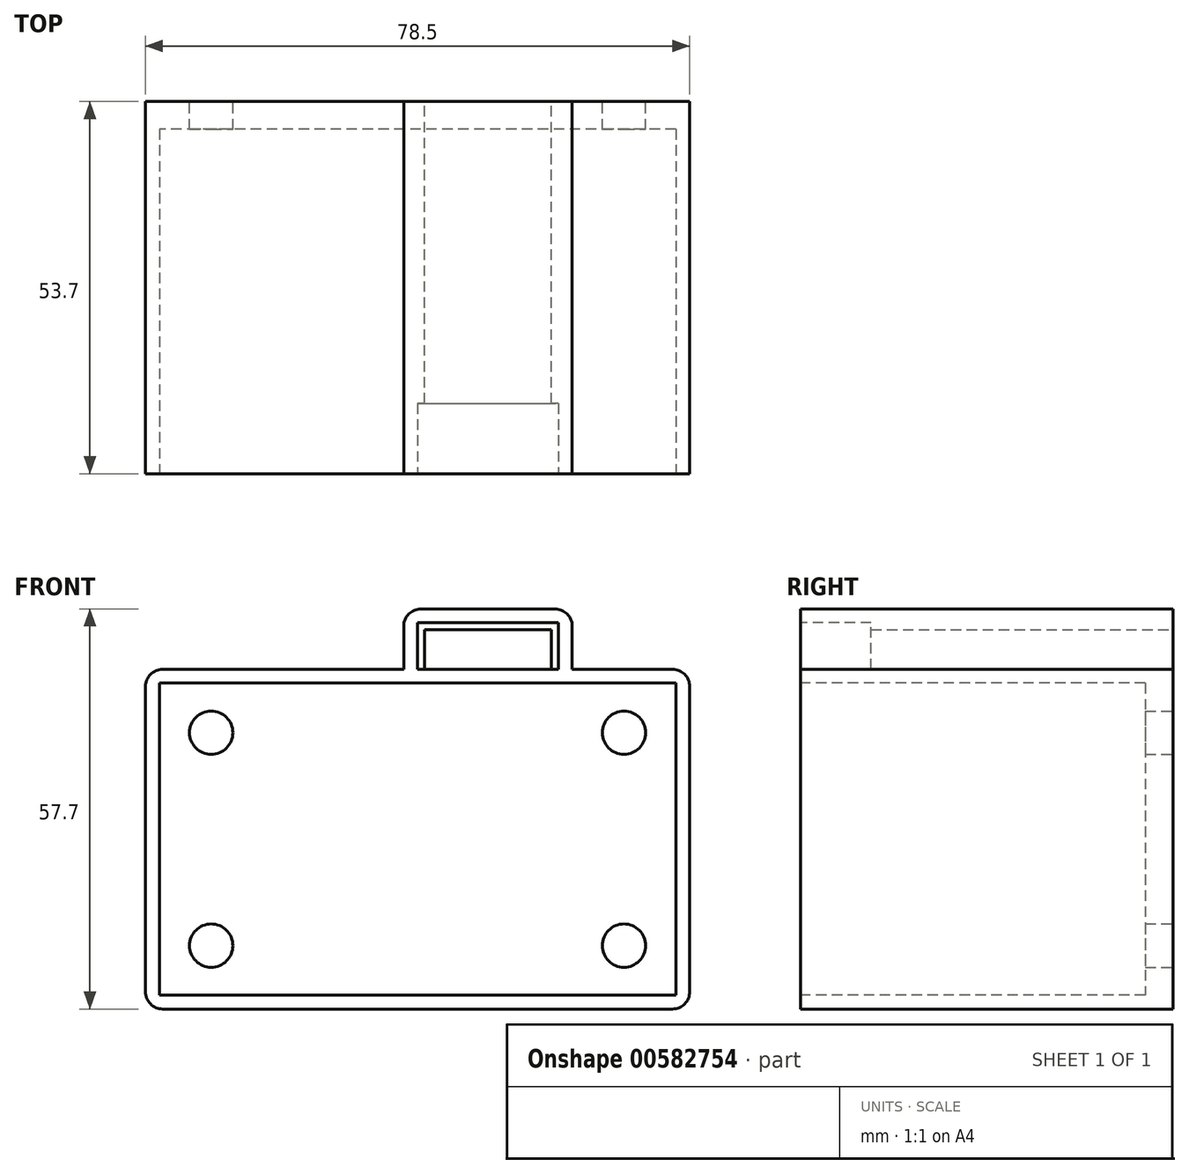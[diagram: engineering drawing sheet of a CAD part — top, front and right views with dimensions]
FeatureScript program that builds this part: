
annotation { "Feature Type Name" : "Feature", "Feature Type Description" : "" }
export const myFeature = defineFeature(function(context is Context, id is Id, definition is map)
    precondition{}
    {
        {
            var Q0;
            Q0=qCreatedBy(makeId("Front.planeOp"),FACE);
            var sketch = newSketch(context, id + "F0", { "sketchPlane" : qUnion([Q0])});
            skLineSegment(sketch, "E0.bottom", {"start": v(37.25, 22.5) * mm, "end": v(-37.25, 22.5) * mm});
            skLineSegment(sketch, "E0.top", {"start": v(37.25, -22.5) * mm, "end": v(-37.25, -22.5) * mm});
            skLineSegment(sketch, "E0.left", {"start": v(37.25, 22.5) * mm, "end": v(37.25, -22.5) * mm});
            skLineSegment(sketch, "E0.right", {"start": v(-37.25, 22.5) * mm, "end": v(-37.25, -22.5) * mm});
            skPoint(sketch, "E0.middle", {"position": v(0, 0) * mm});
            skLineSegment(sketch, "E1.0", {"start": v(39.25, 24.5) * mm, "end": v(-39.25, 24.5) * mm});
            skLineSegment(sketch, "E1.1", {"start": v(39.25, 24.5) * mm, "end": v(39.25, -24.5) * mm});
            skLineSegment(sketch, "E1.2", {"start": v(39.25, -24.5) * mm, "end": v(-39.25, -24.5) * mm});
            skLineSegment(sketch, "E1.3", {"start": v(-39.25, 24.5) * mm, "end": v(-39.25, -24.5) * mm});
            skSolve(sketch);
        }
        {
            var Q0;
            Q0 = qSketchRegion(id + "F0", true);
            extrude(context, id + "F1", {"entities" : qUnion([Q0]), "oppositeDirection" : true, "depth" : 53.7 * mm, "offsetDistance" : 25 * mm});
        }
        {
            var Q0;
            Q0=qCreatedBy(makeId("Front.planeOp"),FACE);
            var sketch = newSketch(context, id + "F2", { "sketchPlane" : qUnion([Q0])});
            skLineSegment(sketch, "E2.bottom", {"start": v(0, 24.5) * mm, "end": v(20.3, 24.5) * mm});
            skLineSegment(sketch, "E2.top", {"start": v(0, 31.2) * mm, "end": v(20.3, 31.2) * mm});
            skLineSegment(sketch, "E2.left", {"start": v(0, 24.5) * mm, "end": v(0, 31.2) * mm});
            skLineSegment(sketch, "E2.right", {"start": v(20.3, 24.5) * mm, "end": v(20.3, 31.2) * mm});
            skLineSegment(sketch, "E3.0", {"start": v(-2, 33.2) * mm, "end": v(22.3, 33.2) * mm});
            skLineSegment(sketch, "E3.1", {"start": v(-2, 22.5) * mm, "end": v(-2, 33.2) * mm});
            skLineSegment(sketch, "E3.2", {"start": v(-2, 22.5) * mm, "end": v(22.3, 22.5) * mm});
            skLineSegment(sketch, "E3.3", {"start": v(22.3, 22.5) * mm, "end": v(22.3, 33.2) * mm});
            skSolve(sketch);
        }
        {
            var Q0;
            Q0 = qSketchRegion(id + "F2", true);
            extrude(context, id + "F3", {"entities" : qUnion([Q0]), "operationType" : NewBodyOperationType.ADD, "oppositeDirection" : true, "depth" : 11.15 * mm, "offsetDistance" : 25 * mm});
        }
        {
            var Q0;
            Q0=makeQuery(id+"F3.opExtrude","CAP_FACE",FACE,{"disambiguationData":[OSD([sQuery(id+"F2.wireOp",EDGE,"E2.bottom"),sQuery(id+"F2.wireOp",EDGE,"E2.top"),sQuery(id+"F2.wireOp",EDGE,"E2.left"),sQuery(id+"F2.wireOp",EDGE,"E2.right"),sQuery(id+"F2.wireOp",EDGE,"E3.0"),sQuery(id+"F2.wireOp",EDGE,"E3.1"),sQuery(id+"F2.wireOp",EDGE,"E3.2"),sQuery(id+"F2.wireOp",EDGE,"E3.3")])],"isStart":false});
            var sketch = newSketch(context, id + "F4", { "sketchPlane" : qUnion([Q0])});
            skLineSegment(sketch, "E4.0", {"start": v(-19.3, 24.5) * mm, "end": v(-19.3, 30.2) * mm});
            skLineSegment(sketch, "E4.1", {"start": v(-1, 30.2) * mm, "end": v(-19.3, 30.2) * mm});
            skLineSegment(sketch, "E4.2", {"start": v(-1, 24.5) * mm, "end": v(-1, 30.2) * mm});
            skLineSegment(sketch, "E5.0", {"start": v(-19.3, 24.5) * mm, "end": v(-1, 24.5) * mm});
            skPoint(sketch, "E6.orphan", {"position": v(-39.25, 24.5) * mm});
            skPoint(sketch, "E7.orphan", {"position": v(39.25, 24.5) * mm});
            skLineSegment(sketch, "E8.0", {"start": v(-20.3, 24.5) * mm, "end": v(-20.3, 31.2) * mm});
            skLineSegment(sketch, "E9.0", {"start": v(0, 31.2) * mm, "end": v(-20.3, 31.2) * mm});
            skLineSegment(sketch, "E10.0", {"start": v(0, 24.5) * mm, "end": v(0, 31.2) * mm});
            skLineSegment(sketch, "E11", {"start": v(-20.3, 24.5) * mm, "end": v(-19.3, 24.5) * mm});
            skLineSegment(sketch, "E12", {"start": v(-1, 24.5) * mm, "end": v(0, 24.5) * mm});
            skSolve(sketch);
        }
        {
            var Q0;
            Q0=makeQuery(id+"F4.imprint","IMPRINT",FACE,{"disambiguationData":[TD([[makeQuery(id+"F4.imprint","IMPRINT",EDGE,{"derivedFrom":sQuery(id+"F4.wireOp",EDGE,"E4.0")}),1.0]])]});
            extrude(context, id + "F5", {"entities" : qUnion([Q0]), "operationType" : NewBodyOperationType.ADD, "oppositeDirection" : true, "depth" : 1 * mm, "offsetDistance" : 25 * mm});
        }
        {
            var Q0;
            Q0=makeQuery(id+"F1.opExtrude","CAP_FACE",FACE,{"disambiguationData":[OSD([sQuery(id+"F0.wireOp",EDGE,"E0.bottom"),sQuery(id+"F0.wireOp",EDGE,"E0.top"),sQuery(id+"F0.wireOp",EDGE,"E0.left"),sQuery(id+"F0.wireOp",EDGE,"E0.right"),sQuery(id+"F0.wireOp",EDGE,"E1.0"),sQuery(id+"F0.wireOp",EDGE,"E1.1"),sQuery(id+"F0.wireOp",EDGE,"E1.2"),sQuery(id+"F0.wireOp",EDGE,"E1.3")])],"isStart":false});
            var sketch = newSketch(context, id + "F6", { "sketchPlane" : qUnion([Q0])});
            skLineSegment(sketch, "E13.0", {"start": v(-37.25, 22.5) * mm, "end": v(37.25, 22.5) * mm});
            skLineSegment(sketch, "E14.0", {"start": v(-37.25, 22.5) * mm, "end": v(-37.25, -22.5) * mm});
            skLineSegment(sketch, "E15.0", {"start": v(-37.25, -22.5) * mm, "end": v(37.25, -22.5) * mm});
            skLineSegment(sketch, "E16.0", {"start": v(37.25, 22.5) * mm, "end": v(37.25, -22.5) * mm});
            skCircle(sketch, "E17", {"center": v(-29.76, 15.36) * mm, "radius": 3.12 * mm});
            skCircle(sketch, "E18.MirrorC", {"center": v(29.76, 15.36) * mm, "radius": 3.12 * mm});
            skCircle(sketch, "E19.MirrorC", {"center": v(29.76, -15.36) * mm, "radius": 3.12 * mm});
            skCircle(sketch, "E20.MirrorC", {"center": v(-29.76, -15.36) * mm, "radius": 3.12 * mm});
            skSolve(sketch);
        }
        {
            var Q0;
            Q0 = qSketchRegion(id + "F6", true);
            extrude(context, id + "F7", {"entities" : qUnion([Q0]), "oppositeDirection" : true, "depth" : 4 * mm, "offsetDistance" : 25 * mm});
        }
        {
            var Q0;
            Q0=makeQuery(id+"F7.opExtrude","SWEPT_BODY",BODY,{"disambiguationData":[OSD([sQuery(id+"F6.wireOp",EDGE,"E13.0"),sQuery(id+"F6.wireOp",EDGE,"E14.0"),sQuery(id+"F6.wireOp",EDGE,"E15.0"),sQuery(id+"F6.wireOp",EDGE,"E16.0"),sQuery(id+"F6.wireOp",EDGE,"E17"),sQuery(id+"F6.wireOp",EDGE,"E18.MirrorC"),sQuery(id+"F6.wireOp",EDGE,"E19.MirrorC"),sQuery(id+"F6.wireOp",EDGE,"E20.MirrorC")])]});
            var Q1;
            Q1=makeQuery(id+"F1.opExtrude","SWEPT_BODY",BODY,{"disambiguationData":[OSD([sQuery(id+"F0.wireOp",EDGE,"E0.bottom"),sQuery(id+"F0.wireOp",EDGE,"E0.top"),sQuery(id+"F0.wireOp",EDGE,"E0.left"),sQuery(id+"F0.wireOp",EDGE,"E0.right"),sQuery(id+"F0.wireOp",EDGE,"E1.0"),sQuery(id+"F0.wireOp",EDGE,"E1.1"),sQuery(id+"F0.wireOp",EDGE,"E1.2"),sQuery(id+"F0.wireOp",EDGE,"E1.3")])]});
            booleanBodies(context, id + "F8", {"operationType" : BooleanOperationType.UNION, "tools" : qUnion([Q0, Q1])});
        }
        {
            var Q0;
            Q0=makeQuery(id+"F5.boolean.opBoolean","MERGE",FACE,{"derivedFrom":[makeQuery(id+"F3.opExtrude","CAP_FACE",FACE,{"disambiguationData":[OSD([sQuery(id+"F2.wireOp",EDGE,"E2.bottom"),sQuery(id+"F2.wireOp",EDGE,"E2.top"),sQuery(id+"F2.wireOp",EDGE,"E2.left"),sQuery(id+"F2.wireOp",EDGE,"E2.right"),sQuery(id+"F2.wireOp",EDGE,"E3.0"),sQuery(id+"F2.wireOp",EDGE,"E3.1"),sQuery(id+"F2.wireOp",EDGE,"E3.2"),sQuery(id+"F2.wireOp",EDGE,"E3.3")])],"isStart":false}),makeQuery(id+"F5.opExtrude","CAP_FACE",FACE,{"disambiguationData":[OSD([sQuery(id+"F4.wireOp",EDGE,"E4.0"),sQuery(id+"F4.wireOp",EDGE,"E4.1"),sQuery(id+"F4.wireOp",EDGE,"E4.2"),sQuery(id+"F4.wireOp",EDGE,"E8.0"),sQuery(id+"F4.wireOp",EDGE,"E9.0"),sQuery(id+"F4.wireOp",EDGE,"E10.0"),sQuery(id+"F4.wireOp",EDGE,"E11"),sQuery(id+"F4.wireOp",EDGE,"E12")])],"isStart":true})]});
            var sketch = newSketch(context, id + "F9", { "sketchPlane" : qUnion([Q0])});
            skLineSegment(sketch, "E21.0", {"start": v(-19.3, 24.5) * mm, "end": v(-19.3, 30.2) * mm});
            skLineSegment(sketch, "E22.0", {"start": v(-1, 30.2) * mm, "end": v(-19.3, 30.2) * mm});
            skLineSegment(sketch, "E23.0", {"start": v(-1, 24.5) * mm, "end": v(-1, 30.2) * mm});
            skLineSegment(sketch, "E24.0", {"start": v(2, 24.5) * mm, "end": v(2, 33.2) * mm});
            skLineSegment(sketch, "E25.0", {"start": v(2, 33.2) * mm, "end": v(-22.3, 33.2) * mm});
            skLineSegment(sketch, "E26.0", {"start": v(-22.3, 24.5) * mm, "end": v(-22.3, 33.2) * mm});
            skLineSegment(sketch, "E27.0", {"start": v(-19.3, 24.5) * mm, "end": v(-22.3, 24.5) * mm});
            skLineSegment(sketch, "E28.0", {"start": v(2, 24.5) * mm, "end": v(-1, 24.5) * mm});
            skSolve(sketch);
        }
        {
            var Q0;
            Q0 = qSketchRegion(id + "F9", true);
            var Q1;
            Q1=makeQuery(id+"F8.opBoolean","MERGE",FACE,{"derivedFrom":[makeQuery(id+"F1.opExtrude","CAP_FACE",FACE,{"disambiguationData":[OSD([sQuery(id+"F0.wireOp",EDGE,"E0.bottom"),sQuery(id+"F0.wireOp",EDGE,"E0.top"),sQuery(id+"F0.wireOp",EDGE,"E0.left"),sQuery(id+"F0.wireOp",EDGE,"E0.right"),sQuery(id+"F0.wireOp",EDGE,"E1.0"),sQuery(id+"F0.wireOp",EDGE,"E1.1"),sQuery(id+"F0.wireOp",EDGE,"E1.2"),sQuery(id+"F0.wireOp",EDGE,"E1.3")])],"isStart":false}),makeQuery(id+"F7.opExtrude","CAP_FACE",FACE,{"disambiguationData":[OSD([sQuery(id+"F6.wireOp",EDGE,"E13.0"),sQuery(id+"F6.wireOp",EDGE,"E14.0"),sQuery(id+"F6.wireOp",EDGE,"E15.0"),sQuery(id+"F6.wireOp",EDGE,"E16.0"),sQuery(id+"F6.wireOp",EDGE,"E17"),sQuery(id+"F6.wireOp",EDGE,"E18.MirrorC"),sQuery(id+"F6.wireOp",EDGE,"E19.MirrorC"),sQuery(id+"F6.wireOp",EDGE,"E20.MirrorC")])],"isStart":true})]});
            extrude(context, id + "F10", {"entities" : qUnion([Q0]), "operationType" : NewBodyOperationType.ADD, "endBound" : BoundingType.UP_TO_SURFACE, "depth" : 25 * mm, "endBoundEntityFace" : qUnion([Q1]), "offsetDistance" : 25 * mm});
        }
        {
            var Q0;
            Q0=makeQuery(id+"F10.boolean.opBoolean","MERGE",EDGE,{"derivedFrom":[makeQuery(id+"F3.opExtrude","SWEPT_EDGE",EDGE,{"disambiguationData":[OSD([sQuery(id+"F2.wireOp",EDGE,"E3.0"),sQuery(id+"F2.wireOp",EDGE,"E3.3")])]}),makeQuery(id+"F10.opExtrude","SWEPT_EDGE",EDGE,{"disambiguationData":[OSD([sQuery(id+"F9.wireOp",EDGE,"E25.0"),sQuery(id+"F9.wireOp",EDGE,"E26.0")])]})]});
            var Q1;
            Q1=makeQuery(id+"F10.boolean.opBoolean","MERGE",EDGE,{"derivedFrom":[makeQuery(id+"F3.opExtrude","SWEPT_EDGE",EDGE,{"disambiguationData":[OSD([sQuery(id+"F2.wireOp",EDGE,"E3.0"),sQuery(id+"F2.wireOp",EDGE,"E3.1")])]}),makeQuery(id+"F10.opExtrude","SWEPT_EDGE",EDGE,{"disambiguationData":[OSD([sQuery(id+"F9.wireOp",EDGE,"E24.0"),sQuery(id+"F9.wireOp",EDGE,"E25.0")])]})]});
            var Q2;
            Q2=makeQuery(id+"F1.opExtrude","SWEPT_EDGE",EDGE,{"disambiguationData":[OSD([sQuery(id+"F0.wireOp",EDGE,"E1.0"),sQuery(id+"F0.wireOp",EDGE,"E1.1")])]});
            var Q3;
            Q3=makeQuery(id+"F1.opExtrude","SWEPT_EDGE",EDGE,{"disambiguationData":[OSD([sQuery(id+"F0.wireOp",EDGE,"E1.1"),sQuery(id+"F0.wireOp",EDGE,"E1.2")])]});
            var Q4;
            Q4=makeQuery(id+"F1.opExtrude","SWEPT_EDGE",EDGE,{"disambiguationData":[OSD([sQuery(id+"F0.wireOp",EDGE,"E1.0"),sQuery(id+"F0.wireOp",EDGE,"E1.3")])]});
            var Q5;
            Q5=makeQuery(id+"F1.opExtrude","SWEPT_EDGE",EDGE,{"disambiguationData":[OSD([sQuery(id+"F0.wireOp",EDGE,"E1.2"),sQuery(id+"F0.wireOp",EDGE,"E1.3")])]});
            fillet(context, id + "F11", {"entities" : qUnion([Q0, Q1, Q2, Q3, Q4, Q5]), "radius" : 2.5 * mm, "tangentPropagation" : true, "allowEdgeOverflow" : false});
        }
    });
